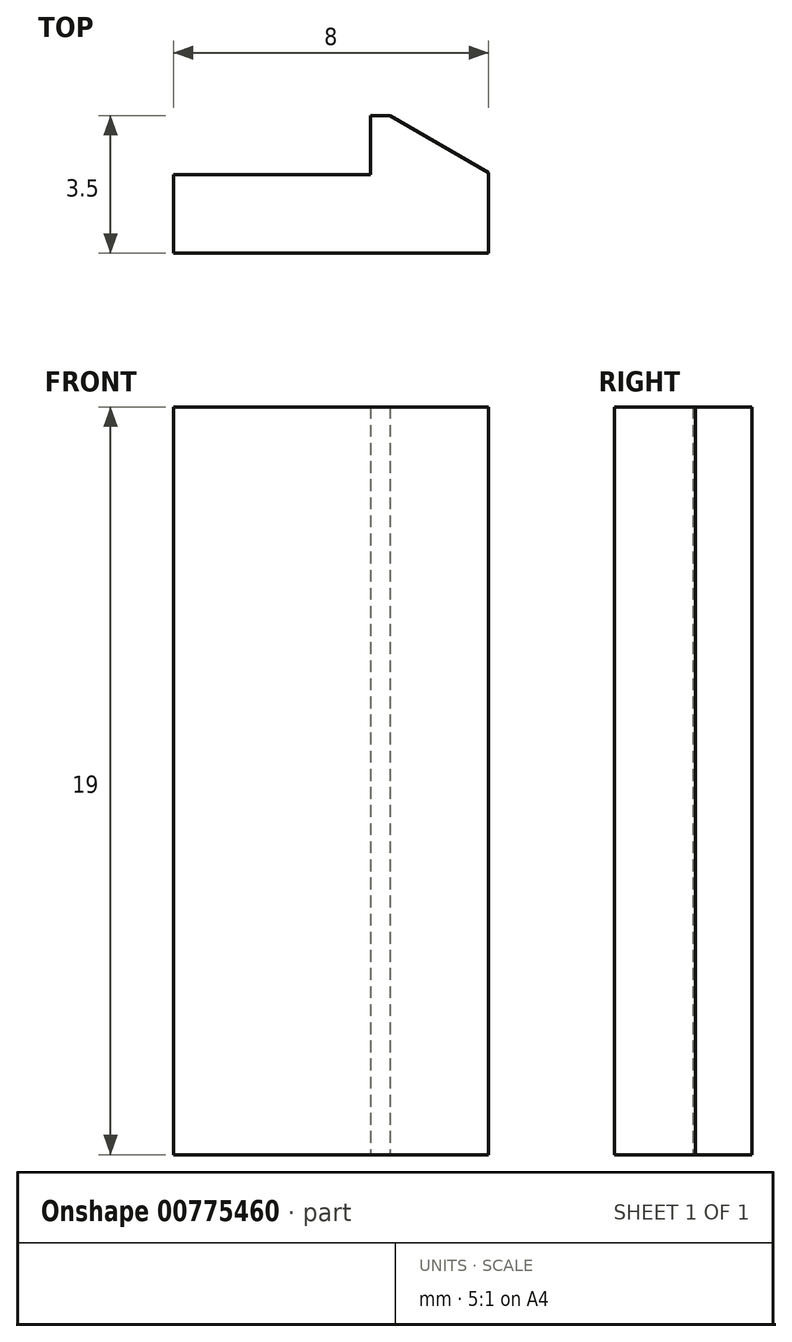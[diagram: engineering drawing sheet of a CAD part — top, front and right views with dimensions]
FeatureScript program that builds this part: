
annotation { "Feature Type Name" : "Feature", "Feature Type Description" : "" }
export const myFeature = defineFeature(function(context is Context, id is Id, definition is map)
    precondition{}
    {
        {
            var Q0;
            Q0=qCreatedBy(makeId("Top.planeOp"),FACE);
            var sketch = newSketch(context, id + "F0", { "sketchPlane" : qUnion([Q0])});
            skLineSegment(sketch, "E0", {"start": v(0, 0) * mm, "end": v(0, 2) * mm});
            skLineSegment(sketch, "E1", {"start": v(0, 2) * mm, "end": v(5, 2) * mm});
            skLineSegment(sketch, "E2", {"start": v(5, 2) * mm, "end": v(5, 3.5) * mm});
            skLineSegment(sketch, "E3", {"start": v(5, 3.5) * mm, "end": v(8, 3.5) * mm});
            skLineSegment(sketch, "E4", {"start": v(8, 3.5) * mm, "end": v(8, 0) * mm});
            skLineSegment(sketch, "E5", {"start": v(8, 0) * mm, "end": v(0, 0) * mm});
            skSolve(sketch);
        }
        {
            var Q0;
            Q0 = qSketchRegion(id + "F0", true);
            extrude(context, id + "F1", {"entities" : qUnion([Q0]), "depth" : 19 * mm, "offsetDistance" : 25 * mm});
        }
        {
            var Q0;
            Q0=makeQuery(id+"F1.opExtrude","SWEPT_EDGE",EDGE,{"disambiguationData":[OSD([sQuery(id+"F0.wireOp",EDGE,"E3"),sQuery(id+"F0.wireOp",EDGE,"E4")])]});
            chamfer(context, id + "F2", {"entities" : qUnion([Q0]), "chamferType" : ChamferType.OFFSET_ANGLE, "width" : 2.5 * mm, "oppositeDirection" : false, "angle" : 30 * degree, "tangentPropagation" : true});
        }
    });
